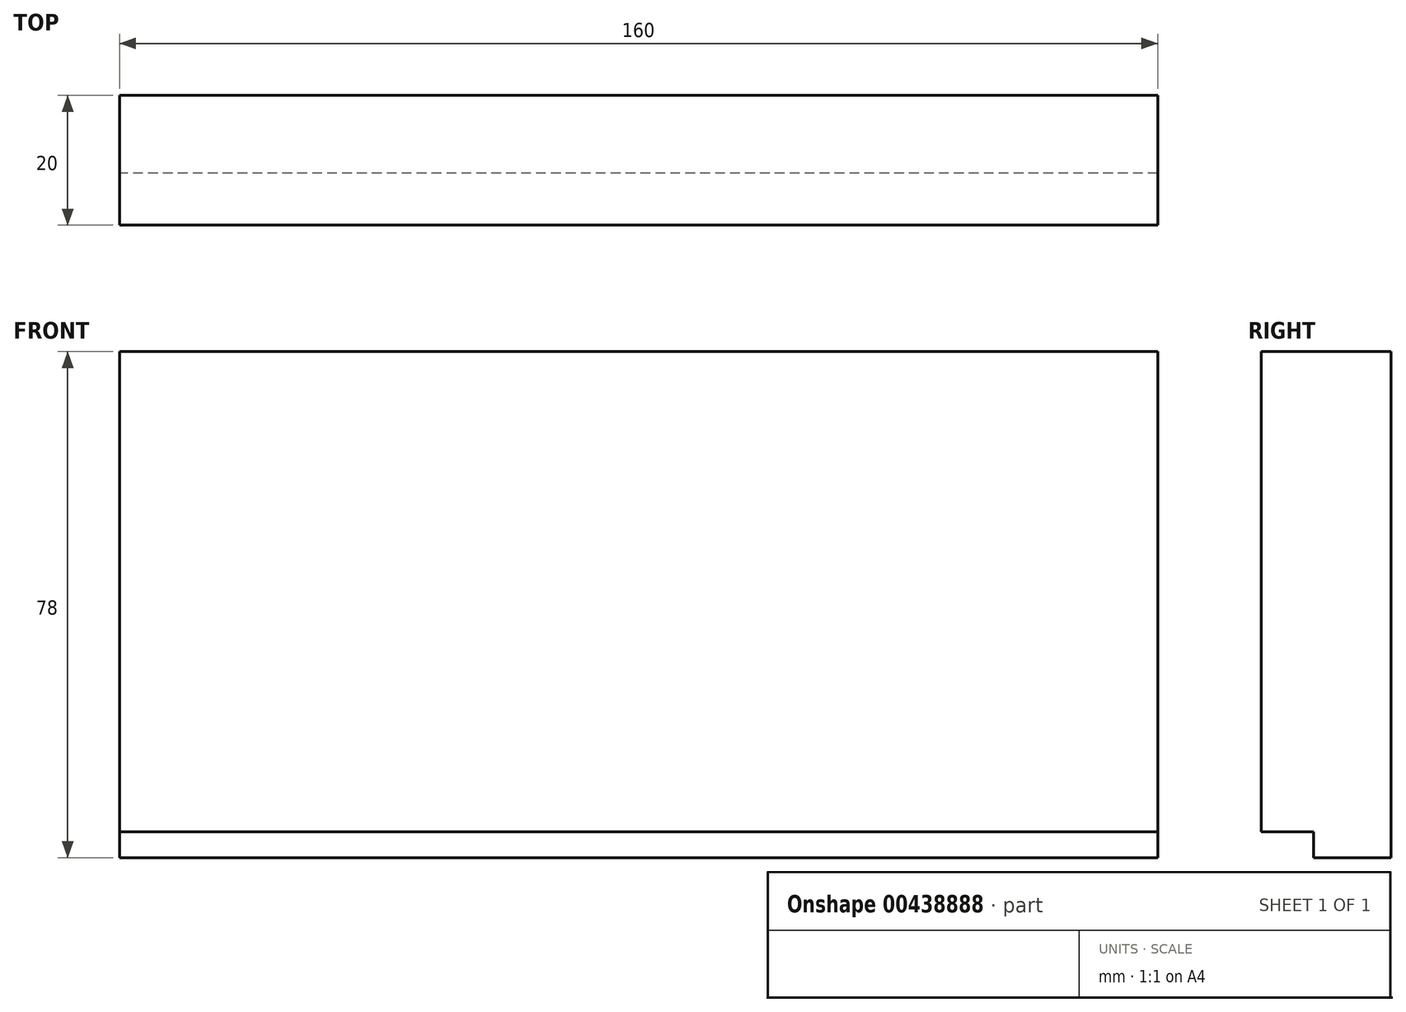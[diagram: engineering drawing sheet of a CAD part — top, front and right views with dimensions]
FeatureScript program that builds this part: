
annotation { "Feature Type Name" : "Feature", "Feature Type Description" : "" }
export const myFeature = defineFeature(function(context is Context, id is Id, definition is map)
    precondition{}
    {
        {
            var Q0;
            Q0=qCreatedBy(makeId("Top.planeOp"),FACE);
            var sketch = newSketch(context, id + "F0", { "sketchPlane" : qUnion([Q0])});
            skLineSegment(sketch, "E0.bottom", {"start": v(-80, 10) * mm, "end": v(80, 10) * mm});
            skLineSegment(sketch, "E0.top", {"start": v(-80, -10) * mm, "end": v(80, -10) * mm});
            skLineSegment(sketch, "E0.left", {"start": v(-80, 10) * mm, "end": v(-80, -10) * mm});
            skLineSegment(sketch, "E0.right", {"start": v(80, 10) * mm, "end": v(80, -10) * mm});
            skPoint(sketch, "E0.middle", {"position": v(0, 0) * mm});
            skLineSegment(sketch, "E1", {"start": v(80, -2) * mm, "end": v(-80, -2) * mm});
            skSolve(sketch);
        }
        {
            var Q0;
            {var subQ0=sQuery(id+"F0.wireOp",EDGE,"E0.bottom");Q0=makeQuery(id+"F0.imprint","IMPRINT",FACE,{"disambiguationData":[TD([[makeQuery(id+"F0.imprint","IMPRINT",EDGE,{"derivedFrom":subQ0}),-1.0]])]});}
            var Q1;
            Q1=sQuery(id+"F0.wireOp",EDGE,"E0.top");
            extrude(context, id + "F1", {"entities" : qUnion([Q0]), "surfaceEntities" : qUnion([Q1]), "oppositeDirection" : true, "depth" : 78 * mm});
        }
        {
            var Q0;
            {var subQ0=sQuery(id+"F0.wireOp",EDGE,"E0.top");Q0=makeQuery(id+"F0.imprint","IMPRINT",FACE,{"disambiguationData":[TD([[makeQuery(id+"F0.imprint","IMPRINT",EDGE,{"derivedFrom":subQ0}),1.0]])]});}
            extrude(context, id + "F2", {"entities" : qUnion([Q0]), "operationType" : NewBodyOperationType.ADD, "oppositeDirection" : true, "depth" : 74 * mm});
        }
    });
